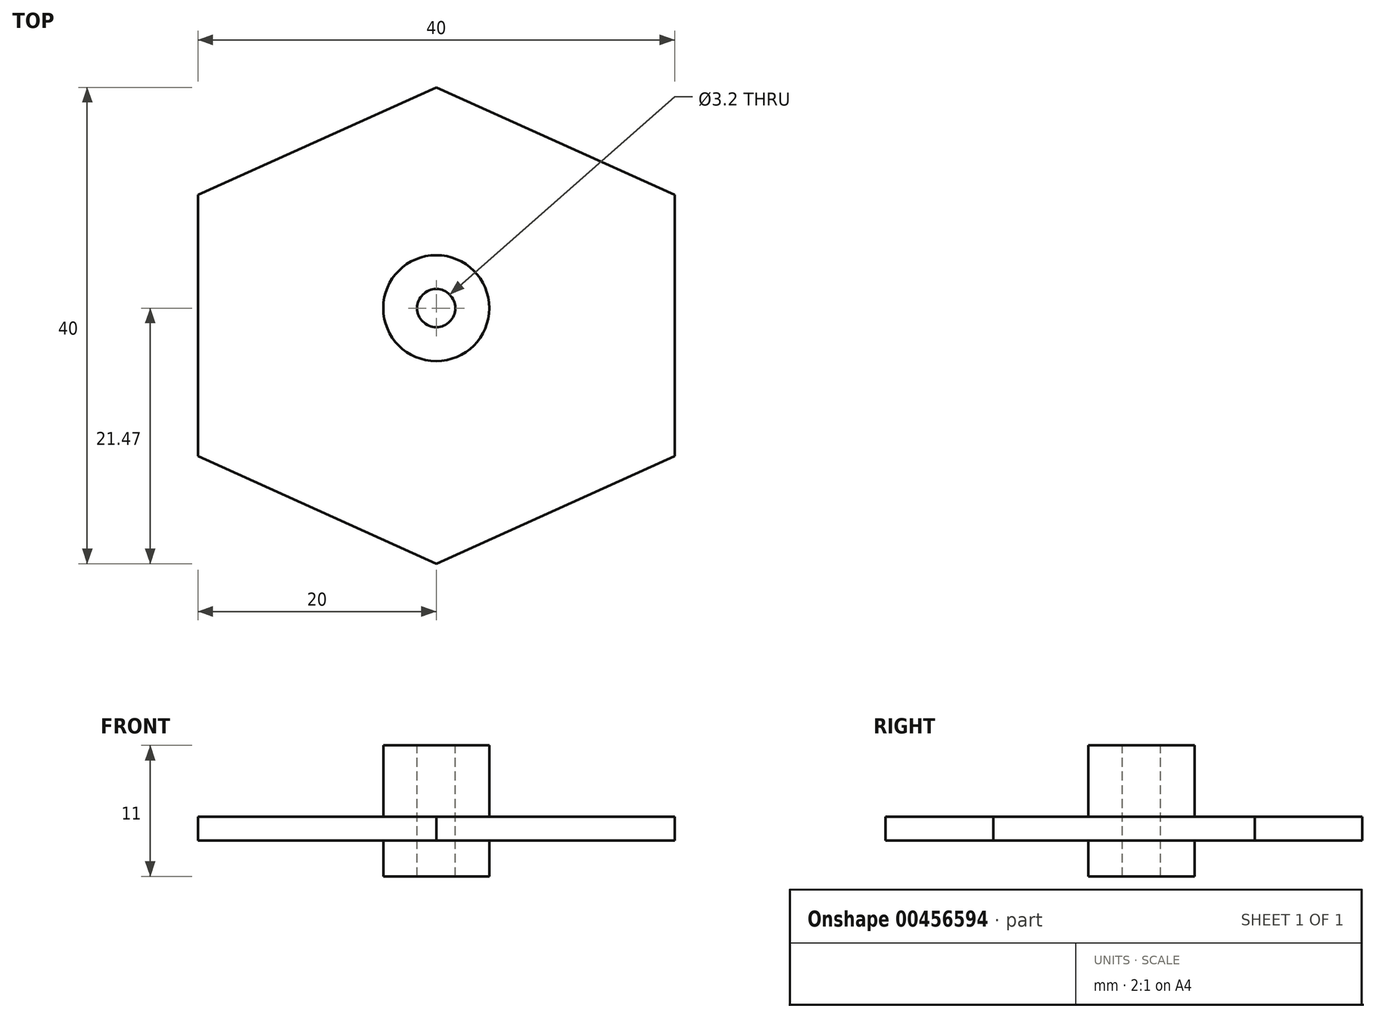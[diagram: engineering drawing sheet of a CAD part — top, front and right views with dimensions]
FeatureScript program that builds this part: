
annotation { "Feature Type Name" : "Feature", "Feature Type Description" : "" }
export const myFeature = defineFeature(function(context is Context, id is Id, definition is map)
    precondition{}
    {
        {
            var Q0;
            Q0=qCreatedBy(makeId("Top.planeOp"),FACE);
            var sketch = newSketch(context, id + "F0", { "sketchPlane" : qUnion([Q0])});
            skLineSegment(sketch, "E0", {"start": v(0, 18.53) * mm, "end": v(-20, 9.5) * mm});
            skLineSegment(sketch, "E1", {"start": v(0, 18.53) * mm, "end": v(20, 9.5) * mm});
            skLineSegment(sketch, "E2", {"start": v(20, 9.5) * mm, "end": v(20, -12.44) * mm});
            skLineSegment(sketch, "E3", {"start": v(-20, 9.5) * mm, "end": v(-20, -12.44) * mm});
            skLineSegment(sketch, "E4", {"start": v(0, -21.47) * mm, "end": v(20, -12.44) * mm});
            skLineSegment(sketch, "E5", {"start": v(-20, -12.44) * mm, "end": v(0, -21.47) * mm});
            skSolve(sketch);
        }
        {
            var Q0;
            Q0 = qSketchRegion(id + "F0", true);
            extrude(context, id + "F1", {"entities" : qUnion([Q0]), "oppositeDirection" : true, "depth" : 2 * mm});
        }
        {
            var Q0;
            Q0=makeQuery(id+"F1.opExtrude","CAP_FACE",FACE,{"disambiguationData":[OSD([sQuery(id+"F0.wireOp",EDGE,"E0"),sQuery(id+"F0.wireOp",EDGE,"E1"),sQuery(id+"F0.wireOp",EDGE,"E2"),sQuery(id+"F0.wireOp",EDGE,"E3"),sQuery(id+"F0.wireOp",EDGE,"E4"),sQuery(id+"F0.wireOp",EDGE,"E5")])],"isStart":true});
            var sketch = newSketch(context, id + "F2", { "sketchPlane" : qUnion([Q0])});
            skCircle(sketch, "E6", {"center": v(0, 0) * mm, "radius": 4.45 * mm});
            skSolve(sketch);
        }
        {
            var Q0;
            Q0 = qSketchRegion(id + "F2", true);
            extrude(context, id + "F3", {"entities" : qUnion([Q0]), "operationType" : NewBodyOperationType.ADD, "depth" : 6 * mm});
        }
        {
            var Q0;
            Q0=makeQuery(id+"F1.opExtrude","CAP_FACE",FACE,{"disambiguationData":[OSD([sQuery(id+"F0.wireOp",EDGE,"E0"),sQuery(id+"F0.wireOp",EDGE,"E1"),sQuery(id+"F0.wireOp",EDGE,"E2"),sQuery(id+"F0.wireOp",EDGE,"E3"),sQuery(id+"F0.wireOp",EDGE,"E4"),sQuery(id+"F0.wireOp",EDGE,"E5")])],"isStart":false});
            var sketch = newSketch(context, id + "F4", { "sketchPlane" : qUnion([Q0])});
            skCircle(sketch, "E7", {"center": v(0, 0) * mm, "radius": 4.45 * mm});
            skSolve(sketch);
        }
        {
            var Q0;
            Q0 = qSketchRegion(id + "F4", true);
            extrude(context, id + "F5", {"entities" : qUnion([Q0]), "operationType" : NewBodyOperationType.ADD, "depth" : 3 * mm});
        }
        {
            var Q0;
            Q0=makeQuery(id+"F3.opExtrude","CAP_FACE",FACE,{"disambiguationData":[OSD([sQuery(id+"F2.wireOp",EDGE,"E6")])],"isStart":false});
            var sketch = newSketch(context, id + "F6", { "sketchPlane" : qUnion([Q0])});
            skCircle(sketch, "E8", {"center": v(0, 0) * mm, "radius": 1.6 * mm});
            skSolve(sketch);
        }
        {
            var Q0;
            Q0 = qSketchRegion(id + "F6", true);
            extrude(context, id + "F7", {"entities" : qUnion([Q0]), "operationType" : NewBodyOperationType.REMOVE, "endBound" : BoundingType.THROUGH_ALL, "oppositeDirection" : true, "depth" : 25 * mm});
        }
    });
